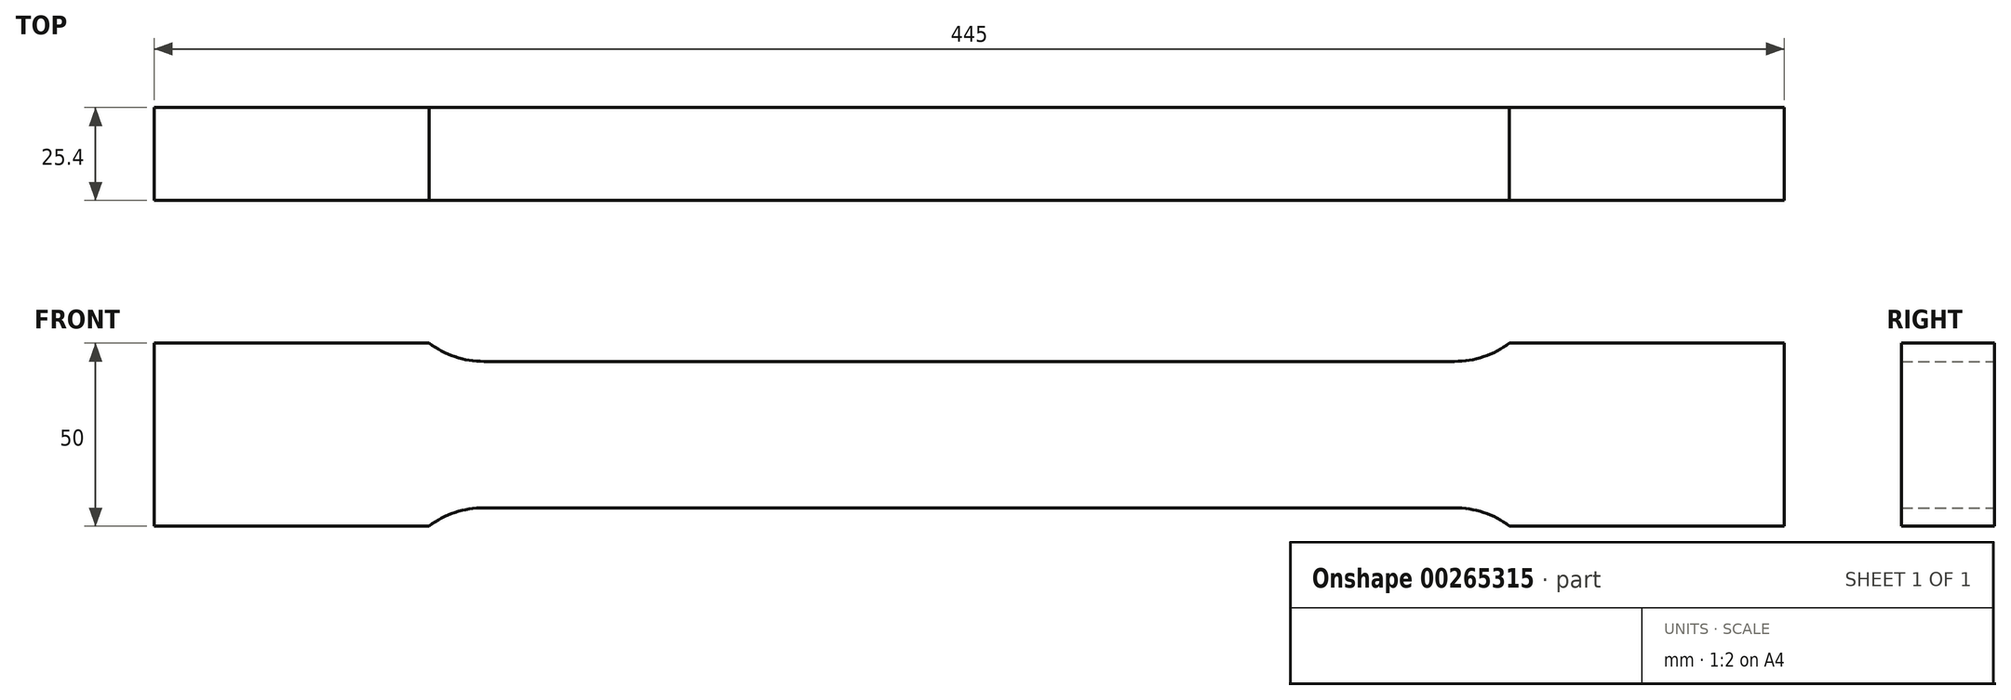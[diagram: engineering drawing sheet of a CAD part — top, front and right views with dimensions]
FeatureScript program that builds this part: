
annotation { "Feature Type Name" : "Feature", "Feature Type Description" : "" }
export const myFeature = defineFeature(function(context is Context, id is Id, definition is map)
    precondition{}
    {
        {
            var Q0;
            Q0=qCreatedBy(makeId("Front.planeOp"),FACE);
            var sketch = newSketch(context, id + "F0", { "sketchPlane" : qUnion([Q0])});
            skLineSegment(sketch, "E0", {"start": v(0, 20) * mm, "end": v(132.5, 20) * mm});
            skArc(sketch, "E1", {"start": v(132.5, 20) * mm, "mid": v(140.4, 21.28) * mm, "end": v(147.5, 25) * mm});
            skLineSegment(sketch, "E2", {"start": v(147.5, 25) * mm, "end": v(222.5, 25) * mm});
            skLineSegment(sketch, "E3", {"start": v(222.5, 25) * mm, "end": v(222.5, 0) * mm});
            skArc(sketch, "E4.MirrorCS", {"start": v(132.5, -20) * mm, "mid": v(140.4, -21.28) * mm, "end": v(147.5, -25) * mm});
            skLineSegment(sketch, "E5.MirrorCS", {"start": v(0, -20) * mm, "end": v(132.5, -20) * mm});
            skLineSegment(sketch, "E6.MirrorCS", {"start": v(222.5, -25) * mm, "end": v(222.5, 0) * mm});
            skLineSegment(sketch, "E7.MirrorCS", {"start": v(147.5, -25) * mm, "end": v(222.5, -25) * mm});
            skLineSegment(sketch, "E8.MirrorCS", {"start": v(-147.5, -25) * mm, "end": v(-222.5, -25) * mm});
            skArc(sketch, "E9.MirrorCS", {"start": v(-132.5, 20) * mm, "mid": v(-140.4, 21.28) * mm, "end": v(-147.5, 25) * mm});
            skLineSegment(sketch, "E10.MirrorCS", {"start": v(-147.5, 25) * mm, "end": v(-222.5, 25) * mm});
            skLineSegment(sketch, "E11.MirrorCS", {"start": v(-222.5, -25) * mm, "end": v(-222.5, 0) * mm});
            skLineSegment(sketch, "E12.MirrorCS", {"start": v(0, -20) * mm, "end": v(-132.5, -20) * mm});
            skArc(sketch, "E13.MirrorCS", {"start": v(-132.5, -20) * mm, "mid": v(-140.4, -21.28) * mm, "end": v(-147.5, -25) * mm});
            skLineSegment(sketch, "E14.MirrorCS", {"start": v(-222.5, 25) * mm, "end": v(-222.5, 0) * mm});
            skLineSegment(sketch, "E15.MirrorCS", {"start": v(0, 20) * mm, "end": v(-132.5, 20) * mm});
            skSolve(sketch);
        }
        {
            var Q0;
            Q0 = qSketchRegion(id + "F0", true);
            extrude(context, id + "F1", {"entities" : qUnion([Q0]), "endBound" : BoundingType.SYMMETRIC, "depth" : 25.4 * mm});
        }
    });
